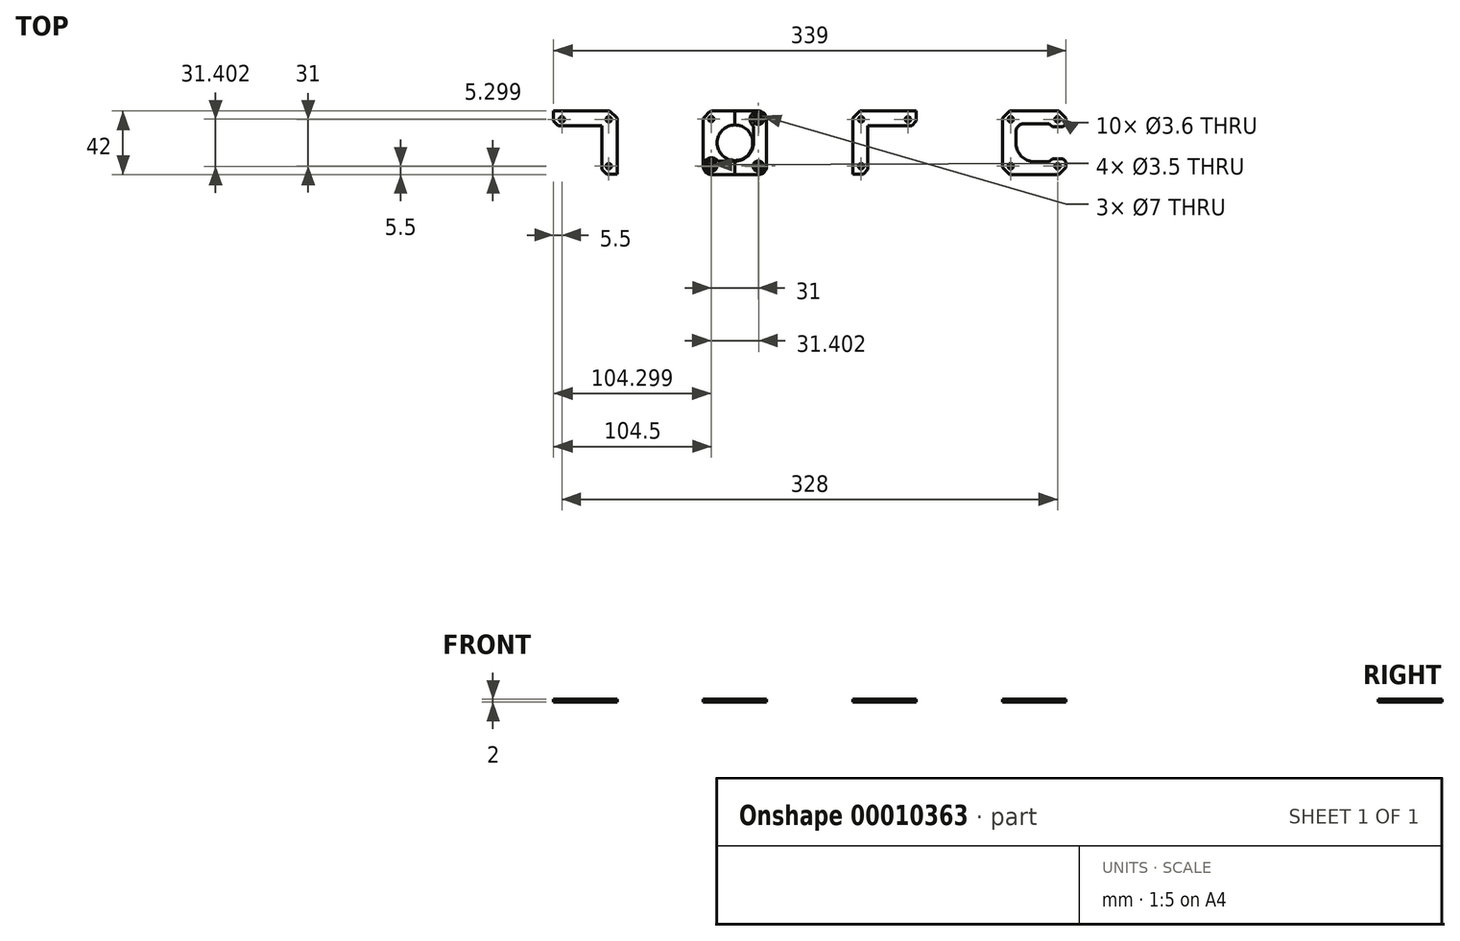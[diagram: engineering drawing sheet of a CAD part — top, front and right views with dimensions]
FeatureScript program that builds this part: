
annotation { "Feature Type Name" : "Feature", "Feature Type Description" : "" }
export const myFeature = defineFeature(function(context is Context, id is Id, definition is map)
    precondition{}
    {
        {
            var Q0;
            Q0=qCreatedBy(makeId("Top.planeOp"),FACE);
            var sketch = newSketch(context, id + "F0", { "sketchPlane" : qUnion([Q0])});
            skLineSegment(sketch, "E0.rect.bottom", {"start": v(15.5, -15.5) * mm, "end": v(-15.5, -15.5) * mm, "construction": true});
            skLineSegment(sketch, "E0.rect.top", {"start": v(15.5, 15.5) * mm, "end": v(-15.5, 15.5) * mm, "construction": true});
            skLineSegment(sketch, "E0.rect.left", {"start": v(15.5, -15.5) * mm, "end": v(15.5, 15.5) * mm, "construction": true});
            skLineSegment(sketch, "E0.rect.right", {"start": v(-15.5, -15.5) * mm, "end": v(-15.5, 15.5) * mm, "construction": true});
            skPoint(sketch, "E0.rect.middle", {"position": v(0, 0) * mm});
            skCircle(sketch, "E1", {"center": v(-15.5, -15.5) * mm, "radius": 3.5 * mm});
            skArc(sketch, "E2", {"start": v(-11.06, -12.25) * mm, "mid": v(-20.4, -13.01) * mm, "end": v(-15.5, -21) * mm});
            skCircle(sketch, "E3", {"center": v(15.5, -15.5) * mm, "radius": 3.5 * mm});
            skCircle(sketch, "E4", {"center": v(15.5, 15.5) * mm, "radius": 3.5 * mm});
            skArc(sketch, "E5", {"start": v(21, 15.5) * mm, "mid": v(13.01, 20.4) * mm, "end": v(12.25, 11.06) * mm});
            skArc(sketch, "E6", {"start": v(0, -12.25) * mm, "mid": v(8.66, -8.66) * mm, "end": v(12.25, 0) * mm});
            skLineSegment(sketch, "E7", {"start": v(0, -12.25) * mm, "end": v(-11.06, -12.25) * mm});
            skLineSegment(sketch, "E8", {"start": v(12.25, 0) * mm, "end": v(12.25, 11.06) * mm});
            skLineSegment(sketch, "E9", {"start": v(-15.5, -21) * mm, "end": v(15.5, -21) * mm});
            skLineSegment(sketch, "E10", {"start": v(21, 15.5) * mm, "end": v(21, -15.5) * mm});
            skArc(sketch, "E11", {"start": v(15.5, -21) * mm, "mid": v(19.39, -19.39) * mm, "end": v(21, -15.5) * mm});
            skLineSegment(sketch, "E12.rect.bottom", {"start": v(83.5, 15.5) * mm, "end": v(114.5, 15.5) * mm, "construction": true});
            skLineSegment(sketch, "E12.rect.top", {"start": v(83.5, -15.5) * mm, "end": v(114.5, -15.5) * mm, "construction": true});
            skLineSegment(sketch, "E12.rect.left", {"start": v(83.5, 15.5) * mm, "end": v(83.5, -15.5) * mm, "construction": true});
            skLineSegment(sketch, "E12.rect.right", {"start": v(114.5, 15.5) * mm, "end": v(114.5, -15.5) * mm, "construction": true});
            skPoint(sketch, "E12.rect.middle", {"position": v(99, 0) * mm});
            skCircle(sketch, "E13", {"center": v(83.5, -15.5) * mm, "radius": 1.8 * mm});
            skCircle(sketch, "E14", {"center": v(83.5, 15.5) * mm, "radius": 1.8 * mm});
            skCircle(sketch, "E15", {"center": v(114.5, 15.5) * mm, "radius": 1.8 * mm});
            skLineSegment(sketch, "E16", {"start": v(117, 11.3) * mm, "end": v(88, 11.3) * mm});
            skLineSegment(sketch, "E17", {"start": v(88, 11.3) * mm, "end": v(88, -17.7) * mm});
            skLineSegment(sketch, "E18", {"start": v(85, -20.7) * mm, "end": v(78, -20.7) * mm});
            skLineSegment(sketch, "E19", {"start": v(78, -20.7) * mm, "end": v(78, 16.2) * mm});
            skLineSegment(sketch, "E20", {"start": v(82.8, 21) * mm, "end": v(120, 21) * mm});
            skLineSegment(sketch, "E21", {"start": v(123, 17.3) * mm, "end": v(123, 21) * mm, "construction": true});
            skLineSegment(sketch, "E22", {"start": v(78, 16.2) * mm, "end": v(82.8, 21) * mm});
            skLineSegment(sketch, "E23", {"start": v(117, 11.3) * mm, "end": v(120, 14.3) * mm});
            skLineSegment(sketch, "E24", {"start": v(85, -20.7) * mm, "end": v(88, -17.7) * mm});
            skLineSegment(sketch, "E25", {"start": v(120, 21) * mm, "end": v(120, 14.3) * mm});
            skLineSegment(sketch, "E26", {"start": v(120, 14.3) * mm, "end": v(123, 17.3) * mm, "construction": true});
            skLineSegment(sketch, "E27", {"start": v(120, 21) * mm, "end": v(123, 21) * mm, "construction": true});
            skLineSegment(sketch, "E28.rect.bottom", {"start": v(182.5, -15.5) * mm, "end": v(213.5, -15.5) * mm, "construction": true});
            skLineSegment(sketch, "E28.rect.top", {"start": v(182.5, 15.5) * mm, "end": v(213.5, 15.5) * mm, "construction": true});
            skLineSegment(sketch, "E28.rect.left", {"start": v(182.5, -15.5) * mm, "end": v(182.5, 15.5) * mm, "construction": true});
            skLineSegment(sketch, "E28.rect.right", {"start": v(213.5, -15.5) * mm, "end": v(213.5, 15.5) * mm, "construction": true});
            skPoint(sketch, "E28.rect.middle", {"position": v(198, 0) * mm});
            skCircle(sketch, "E29", {"center": v(182.5, -15.5) * mm, "radius": 1.8 * mm});
            skCircle(sketch, "E30", {"center": v(182.5, 15.5) * mm, "radius": 1.8 * mm});
            skCircle(sketch, "E31", {"center": v(213.5, 15.5) * mm, "radius": 1.8 * mm});
            skCircle(sketch, "E32", {"center": v(213.5, -15.5) * mm, "radius": 1.8 * mm});
            skLineSegment(sketch, "E33", {"start": v(186, 7.5) * mm, "end": v(186, -0.5) * mm});
            skLineSegment(sketch, "E34.trimOffspring", {"start": v(198, -12.5) * mm, "end": v(208, -12.5) * mm});
            skPoint(sketch, "E35.visualSharp", {"position": v(186, -12.5) * mm});
            skArc(sketch, "E35.filletArc", {"start": v(186, -0.5) * mm, "mid": v(189.51, -8.99) * mm, "end": v(198, -12.5) * mm});
            skLineSegment(sketch, "E36.rect.bottom", {"start": v(177, -21) * mm, "end": v(219, -21) * mm});
            skLineSegment(sketch, "E36.rect.top", {"start": v(177, 21) * mm, "end": v(219, 21) * mm});
            skLineSegment(sketch, "E36.rect.left", {"start": v(177, -21) * mm, "end": v(177, 21) * mm});
            skLineSegment(sketch, "E36.rect.right", {"start": v(219, -21) * mm, "end": v(219, -12.5) * mm});
            skLineSegment(sketch, "E37", {"start": v(210, -10.5) * mm, "end": v(217, -10.5) * mm});
            skLineSegment(sketch, "E38", {"start": v(217, -10.5) * mm, "end": v(219, -12.5) * mm});
            skLineSegment(sketch, "E39.0.MirrorCS", {"start": v(210, -10.5) * mm, "end": v(208, -12.5) * mm});
            skLineSegment(sketch, "E40", {"start": v(198, 0) * mm, "end": v(177, 0) * mm, "construction": true});
            skLineSegment(sketch, "E41.0.MirrorCS", {"start": v(156, 0) * mm, "end": v(177, 0) * mm, "construction": true});
            skLineSegment(sketch, "E42.0.MirrorCS", {"start": v(191, 12.5) * mm, "end": v(208, 12.5) * mm});
            skLineSegment(sketch, "E43.0.MirrorCS", {"start": v(210, 10.5) * mm, "end": v(208, 12.5) * mm});
            skLineSegment(sketch, "E44.0.MirrorCS", {"start": v(210, 10.5) * mm, "end": v(217, 10.5) * mm});
            skLineSegment(sketch, "E45.0.MirrorCS", {"start": v(217, 10.5) * mm, "end": v(219, 12.5) * mm});
            skLineSegment(sketch, "E46.0.MirrorCS", {"start": v(219, 21) * mm, "end": v(219, 12.5) * mm});
            skLineSegment(sketch, "E47.rect.bottom", {"start": v(198, 37.2) * mm, "end": v(160.8, 0) * mm});
            skLineSegment(sketch, "E47.rect.top", {"start": v(235.2, 0) * mm, "end": v(198, -37.2) * mm});
            skLineSegment(sketch, "E47.rect.left", {"start": v(198, 37.2) * mm, "end": v(235.2, 0) * mm});
            skLineSegment(sketch, "E47.rect.right", {"start": v(160.8, 0) * mm, "end": v(198, -37.2) * mm});
            skPoint(sketch, "E48", {"position": v(181.8, 21) * mm});
            skPoint(sketch, "E49.visualSharp", {"position": v(186, 12.5) * mm});
            skArc(sketch, "E49.filletArc", {"start": v(191, 12.5) * mm, "mid": v(187.46, 11.04) * mm, "end": v(186, 7.5) * mm});
            skSolve(sketch);
        }
        {
            var Q0;
            Q0=makeQuery(id+"F0.imprint","IMPRINT",FACE,{"disambiguationData":[TD([[makeQuery(id+"F0.imprint","IMPRINT",EDGE,{"derivedFrom":sQuery(id+"F0.wireOp",EDGE,"E1")}),-1.0]])]});
            var Q1;
            Q1=makeQuery(id+"F0.imprint","IMPRINT",FACE,{"disambiguationData":[TD([[makeQuery(id+"F0.imprint","IMPRINT",EDGE,{"derivedFrom":sQuery(id+"F0.wireOp",EDGE,"E13")}),-1.0]])]});
            var Q2;
            Q2=makeQuery(id+"F0.imprint","IMPRINT",FACE,{"disambiguationData":[TD([[makeQuery(id+"F0.imprint","IMPRINT",EDGE,{"derivedFrom":sQuery(id+"F0.wireOp",EDGE,"E29")}),-1.0]])]});
            extrude(context, id + "F1", {"entities" : qUnion([Q0, Q1, Q2]), "depth" : 2 * mm});
        }
        {
            var Q0;
            Q0=makeQuery(id+"F1.opExtrude","SWEPT_BODY",BODY,{"disambiguationData":[OSD([sQuery(id+"F0.wireOp",EDGE,"E13"),sQuery(id+"F0.wireOp",EDGE,"E14"),sQuery(id+"F0.wireOp",EDGE,"E15"),sQuery(id+"F0.wireOp",EDGE,"E16"),sQuery(id+"F0.wireOp",EDGE,"E17"),sQuery(id+"F0.wireOp",EDGE,"E18"),sQuery(id+"F0.wireOp",EDGE,"E19"),sQuery(id+"F0.wireOp",EDGE,"E20"),sQuery(id+"F0.wireOp",EDGE,"E22"),sQuery(id+"F0.wireOp",EDGE,"E23"),sQuery(id+"F0.wireOp",EDGE,"E24"),sQuery(id+"F0.wireOp",EDGE,"E25")])]});
            var Q1;
            Q1=qCreatedBy(makeId("Right.planeOp"),FACE);
            mirror(context, id + "F2", {"entities" : qUnion([Q0]), "mirrorPlane" : qUnion([Q1])});
        }
        {
            var Q0;
            Q0=qCreatedBy(makeId("Top.planeOp"),FACE);
            var sketch = newSketch(context, id + "F3", { "sketchPlane" : qUnion([Q0])});
            skLineSegment(sketch, "E50.rect.bottom", {"start": v(14.96, -21) * mm, "end": v(0, -21) * mm});
            skLineSegment(sketch, "E50.rect.top", {"start": v(14.96, 21) * mm, "end": v(0, 21) * mm});
            skLineSegment(sketch, "E50.rect.left", {"start": v(21, -14.96) * mm, "end": v(21, 14.96) * mm});
            skLineSegment(sketch, "E51", {"start": v(17.08, 20.12) * mm, "end": v(20.12, 17.08) * mm});
            skLineSegment(sketch, "E52", {"start": v(0, 21) * mm, "end": v(0, -21) * mm, "construction": true});
            skLineSegment(sketch, "E53", {"start": v(-21, 0) * mm, "end": v(21, 0) * mm, "construction": true});
            skLineSegment(sketch, "E54.0.MirrorCS", {"start": v(17.08, -20.12) * mm, "end": v(20.12, -17.08) * mm});
            skLineSegment(sketch, "E55", {"start": v(0, 0) * mm, "end": v(21, 21) * mm, "construction": true});
            skCircle(sketch, "E56", {"center": v(15.7, 15.7) * mm, "radius": 1.75 * mm});
            skCircle(sketch, "E57.0.MirrorC", {"center": v(15.7, -15.7) * mm, "radius": 1.75 * mm});
            skArc(sketch, "E58.trimOffspring", {"start": v(0, -11.8) * mm, "mid": v(11.8, 0) * mm, "end": v(0, 11.8) * mm});
            skPoint(sketch, "E59.visualSharp", {"position": v(16.2, 21) * mm});
            skArc(sketch, "E59.filletArc", {"start": v(17.08, 20.12) * mm, "mid": v(16.1, 20.77) * mm, "end": v(14.96, 21) * mm});
            skPoint(sketch, "E60.visualSharp", {"position": v(21, 16.2) * mm});
            skArc(sketch, "E60.filletArc", {"start": v(21, 14.96) * mm, "mid": v(20.77, 16.1) * mm, "end": v(20.12, 17.08) * mm});
            skPoint(sketch, "E61.visualSharp", {"position": v(21, -16.2) * mm});
            skArc(sketch, "E61.filletArc", {"start": v(20.12, -17.08) * mm, "mid": v(20.77, -16.1) * mm, "end": v(21, -14.96) * mm});
            skPoint(sketch, "E62.visualSharp", {"position": v(16.2, -21) * mm});
            skArc(sketch, "E62.filletArc", {"start": v(14.96, -21) * mm, "mid": v(16.1, -20.77) * mm, "end": v(17.08, -20.12) * mm});
            skLineSegment(sketch, "E63", {"start": v(0, 11.8) * mm, "end": v(0, 21) * mm});
            skLineSegment(sketch, "E64", {"start": v(0, -11.8) * mm, "end": v(0, -21) * mm});
            skSolve(sketch);
        }
        {
            var Q0;
            Q0=makeQuery(id+"F3.imprint","IMPRINT",FACE,{"disambiguationData":[TD([[makeQuery(id+"F3.imprint","IMPRINT",EDGE,{"derivedFrom":sQuery(id+"F3.wireOp",EDGE,"E50.rect.bottom")}),-1.0]])]});
            extrude(context, id + "F4", {"entities" : qUnion([Q0]), "depth" : 2 * mm});
        }
        {
            var Q0;
            Q0=makeQuery(id+"F4.opExtrude","SWEPT_BODY",BODY,{"disambiguationData":[OSD([sQuery(id+"F3.wireOp",EDGE,"E50.rect.bottom"),sQuery(id+"F3.wireOp",EDGE,"E50.rect.top"),sQuery(id+"F3.wireOp",EDGE,"E50.rect.left"),sQuery(id+"F3.wireOp",EDGE,"E51"),sQuery(id+"F3.wireOp",EDGE,"E54.0.MirrorCS"),sQuery(id+"F3.wireOp",EDGE,"E56"),sQuery(id+"F3.wireOp",EDGE,"E57.0.MirrorC"),sQuery(id+"F3.wireOp",EDGE,"E58.trimOffspring"),sQuery(id+"F3.wireOp",EDGE,"E59.filletArc"),sQuery(id+"F3.wireOp",EDGE,"E60.filletArc"),sQuery(id+"F3.wireOp",EDGE,"E61.filletArc"),sQuery(id+"F3.wireOp",EDGE,"E62.filletArc"),sQuery(id+"F3.wireOp",EDGE,"E63"),sQuery(id+"F3.wireOp",EDGE,"E64")])]});
            var Q1;
            Q1=makeQuery(id+"F4.opExtrude","SWEPT_FACE",FACE,{"disambiguationData":[OSD([sQuery(id+"F3.wireOp",EDGE,"E63")])]});
            mirror(context, id + "F5", {"entities" : qUnion([Q0]), "mirrorPlane" : qUnion([Q1])});
        }
    });
